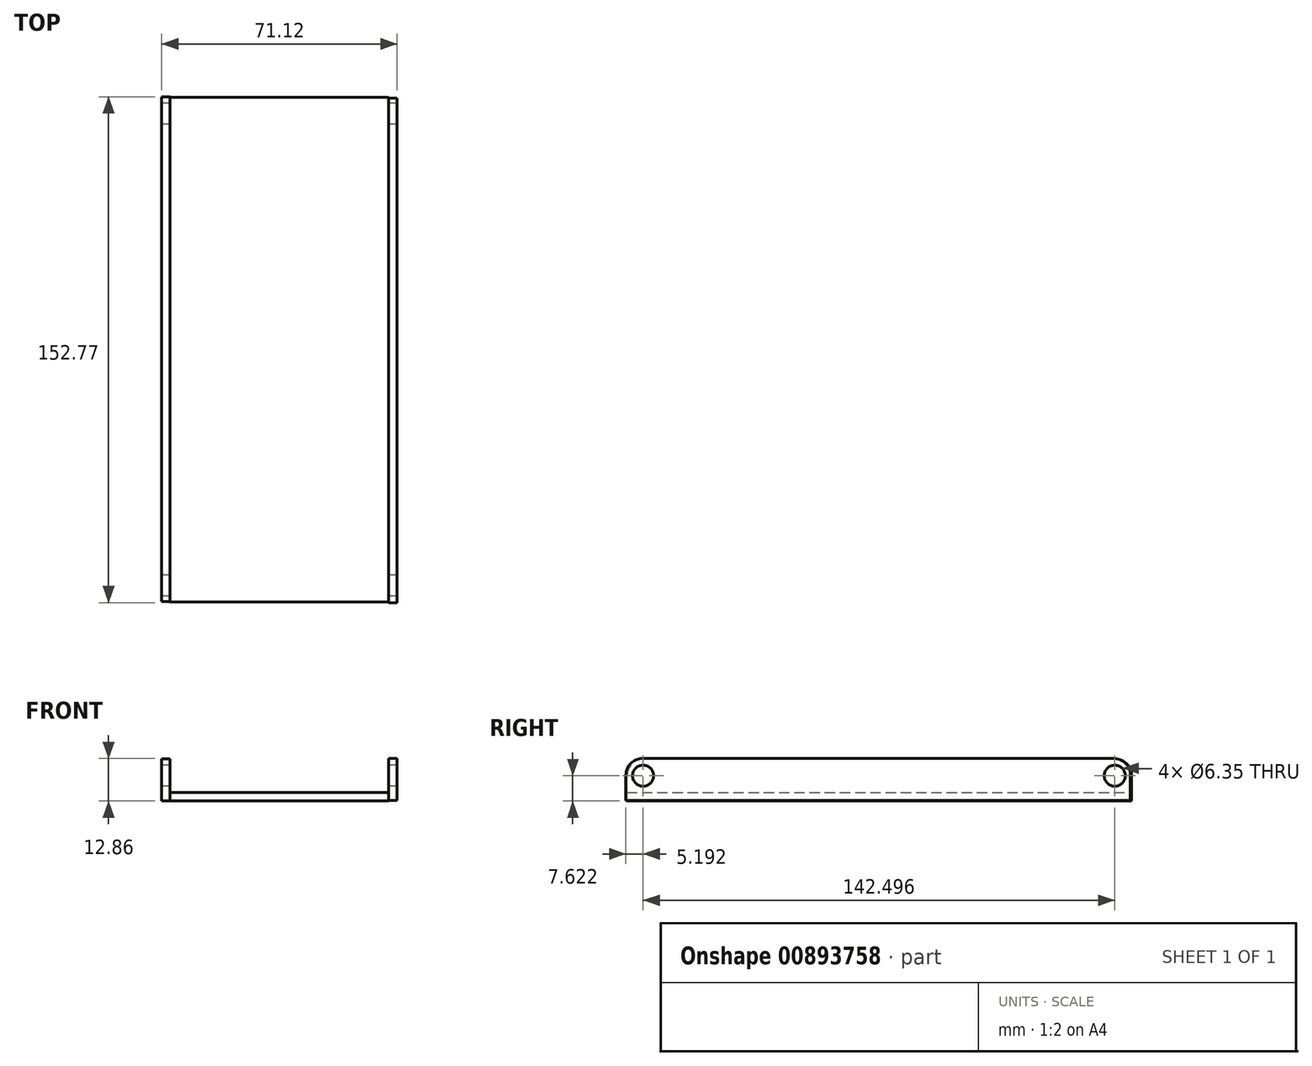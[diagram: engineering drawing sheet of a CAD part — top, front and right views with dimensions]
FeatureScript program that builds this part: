
annotation { "Feature Type Name" : "Feature", "Feature Type Description" : "" }
export const myFeature = defineFeature(function(context is Context, id is Id, definition is map)
    precondition{}
    {
        {
            var Q0;
            Q0=qCreatedBy(makeId("Top.planeOp"),FACE);
            var sketch = newSketch(context, id + "F0", { "sketchPlane" : qUnion([Q0])});
            skLineSegment(sketch, "E0.bottom", {"start": v(33.02, -76.2) * mm, "end": v(-33.02, -76.2) * mm});
            skLineSegment(sketch, "E0.top", {"start": v(33.02, 76.2) * mm, "end": v(-33.02, 76.2) * mm});
            skLineSegment(sketch, "E0.left", {"start": v(33.02, -76.2) * mm, "end": v(33.02, 76.2) * mm});
            skLineSegment(sketch, "E0.right", {"start": v(-33.02, -76.2) * mm, "end": v(-33.02, 76.2) * mm});
            skPoint(sketch, "E0.middle", {"position": v(0, 0) * mm});
            skSolve(sketch);
        }
        {
            var Q0;
            Q0 = qSketchRegion(id + "F0", true);
            extrude(context, id + "F1", {"entities" : qUnion([Q0]), "depth" : 2.54 * mm, "offsetDistance" : 25.4 * mm});
        }
        {
            var Q0;
            Q0=makeQuery(id+"F1.opExtrude","SWEPT_FACE",FACE,{"disambiguationData":[OSD([sQuery(id+"F0.wireOp",EDGE,"E0.left")])]});
            var sketch = newSketch(context, id + "F2", { "sketchPlane" : qUnion([Q0])});
            skLineSegment(sketch, "E1.bottom", {"start": v(75.96, 0.1) * mm, "end": v(-76.44, 0.1) * mm});
            skLineSegment(sketch, "E1.top", {"start": v(75.96, 12.8) * mm, "end": v(-76.44, 12.8) * mm});
            skLineSegment(sketch, "E1.left", {"start": v(75.96, 0.1) * mm, "end": v(75.96, 12.8) * mm});
            skLineSegment(sketch, "E1.right", {"start": v(-76.44, 0.1) * mm, "end": v(-76.44, 12.8) * mm});
            skPoint(sketch, "E1.middle", {"position": v(-0.24, 6.45) * mm});
            skSolve(sketch);
        }
        {
            var Q0;
            Q0 = qSketchRegion(id + "F2", true);
            extrude(context, id + "F3", {"entities" : qUnion([Q0]), "operationType" : NewBodyOperationType.ADD, "depth" : 2.54 * mm, "offsetDistance" : 25.4 * mm});
        }
        {
            var Q0;
            Q0=makeQuery(id+"F1.opExtrude","SWEPT_FACE",FACE,{"disambiguationData":[OSD([sQuery(id+"F0.wireOp",EDGE,"E0.right")])]});
            var sketch = newSketch(context, id + "F4", { "sketchPlane" : qUnion([Q0])});
            skLineSegment(sketch, "E2.bottom", {"start": v(76.07, -0.06) * mm, "end": v(-76.33, -0.06) * mm});
            skLineSegment(sketch, "E2.top", {"start": v(76.07, 12.64) * mm, "end": v(-76.33, 12.64) * mm});
            skLineSegment(sketch, "E2.left", {"start": v(76.07, -0.06) * mm, "end": v(76.07, 12.64) * mm});
            skLineSegment(sketch, "E2.right", {"start": v(-76.33, -0.06) * mm, "end": v(-76.33, 12.64) * mm});
            skPoint(sketch, "E2.middle", {"position": v(-0.13, 6.3) * mm});
            skSolve(sketch);
        }
        {
            var Q0;
            Q0 = qSketchRegion(id + "F4", true);
            extrude(context, id + "F5", {"entities" : qUnion([Q0]), "operationType" : NewBodyOperationType.ADD, "depth" : 2.54 * mm, "offsetDistance" : 25.4 * mm});
        }
        {
            var Q0;
            Q0=makeQuery(id+"F3.opExtrude","SWEPT_EDGE",EDGE,{"disambiguationData":[OSD([sQuery(id+"F2.wireOp",EDGE,"E1.top"),sQuery(id+"F2.wireOp",EDGE,"E1.right")])]});
            var Q1;
            Q1=makeQuery(id+"F5.opExtrude","SWEPT_EDGE",EDGE,{"disambiguationData":[OSD([sQuery(id+"F4.wireOp",EDGE,"E2.top"),sQuery(id+"F4.wireOp",EDGE,"E2.left")])]});
            var Q2;
            Q2=makeQuery(id+"F3.opExtrude","SWEPT_EDGE",EDGE,{"disambiguationData":[OSD([sQuery(id+"F2.wireOp",EDGE,"E1.top"),sQuery(id+"F2.wireOp",EDGE,"E1.left")])]});
            var Q3;
            Q3=makeQuery(id+"F5.opExtrude","SWEPT_EDGE",EDGE,{"disambiguationData":[OSD([sQuery(id+"F4.wireOp",EDGE,"E2.top"),sQuery(id+"F4.wireOp",EDGE,"E2.right")])]});
            fillet(context, id + "F6", {"entities" : qUnion([Q0, Q1, Q2, Q3]), "radius" : 5.08 * mm, "tangentPropagation" : true, "allowEdgeOverflow" : false});
        }
        {
            var Q0;
            Q0=makeQuery(id+"F5.opExtrude","CAP_FACE",FACE,{"disambiguationData":[OSD([sQuery(id+"F4.wireOp",EDGE,"E2.bottom"),sQuery(id+"F4.wireOp",EDGE,"E2.top"),sQuery(id+"F4.wireOp",EDGE,"E2.left"),sQuery(id+"F4.wireOp",EDGE,"E2.right")])],"isStart":false});
            var sketch = newSketch(context, id + "F7", { "sketchPlane" : qUnion([Q0])});
            skCircle(sketch, "E3", {"center": v(-71.25, 7.56) * mm, "radius": 3.18 * mm});
            skCircle(sketch, "E4.MirrorC", {"center": v(71.25, 7.56) * mm, "radius": 3.18 * mm});
            skSolve(sketch);
        }
        {
            var Q0;
            Q0 = qSketchRegion(id + "F7", true);
            extrude(context, id + "F8", {"entities" : qUnion([Q0]), "operationType" : NewBodyOperationType.REMOVE, "oppositeDirection" : true, "depth" : 90.17 * mm, "offsetDistance" : 25.4 * mm});
        }
    });
